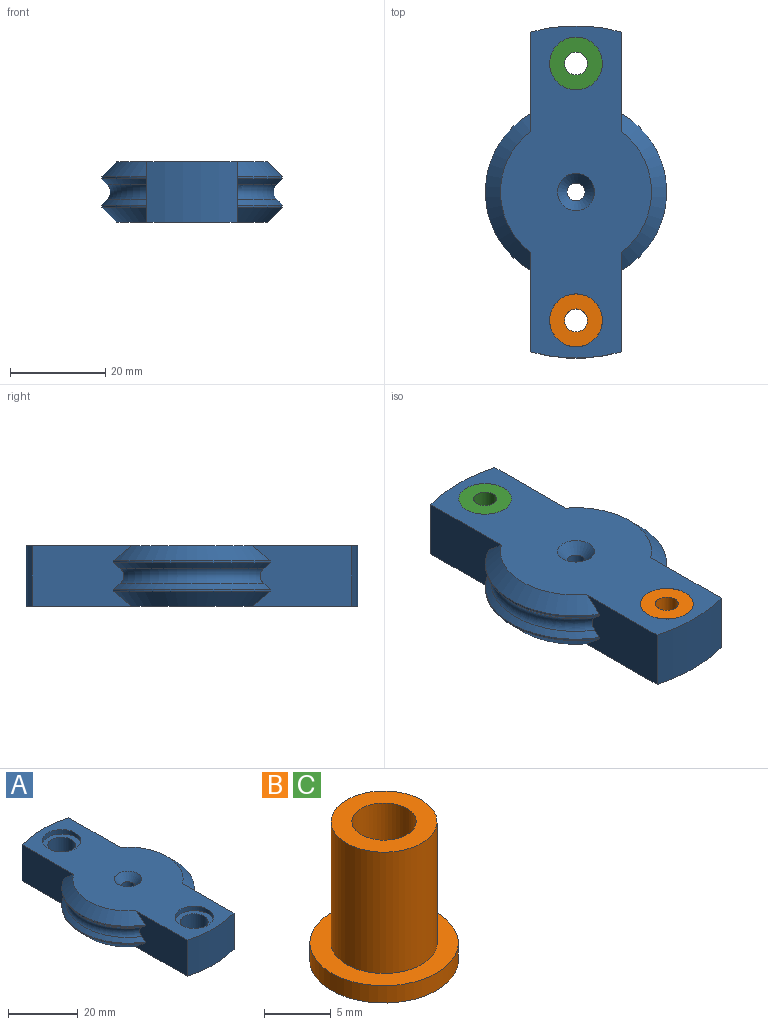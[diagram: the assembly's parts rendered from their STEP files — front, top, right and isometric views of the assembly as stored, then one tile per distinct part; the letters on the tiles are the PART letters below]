
ASSEMBLY  parts=3 mates=2
PART A: 37 faces, bbox 42.2x69.9x12.7 mm
  f0: cylinder r=19.05mm len=33mm, axis (0,0,1), area 14.8mm2, adj f3,f12,f25,f29
  f1: cylinder r=19.05mm len=33mm, axis (0,0,1), area 14.8mm2, adj f8,f14,f23,f26
  f2: plane 69.85x31.75mm, normal (0,0,-1), area 1405.3mm2, adj f3,f6,f8,f9,f12,f13,f14,f15
  f3: plane 20.93x12.73mm, normal (1,0,0), area 237mm2, adj f0,f2,f4,f5,f6,f24,f25,f27
  f4: cylinder r=19.05mm len=33mm, axis (0,0,1), area 14.8mm2, adj f3,f12,f24,f27
  f5: plane 69.85x31.75mm, normal (0,0,1), area 1297.7mm2, adj f3,f6,f8,f11,f12,f13,f14,f17
  f6: cylinder r=34.92mm len=19.05mm, axis (0,0,1), area 245mm2, adj f2,f3,f5,f8
  f7: cylinder r=19.05mm len=33mm, axis (0,0,1), area 14.8mm2, adj f8,f14,f22,f28
  f8: plane 20.93x12.73mm, normal (-1,0,0), area 237mm2, adj f1,f2,f5,f6,f7,f22,f23,f26
  f9: cylinder r=3.99mm len=11.11mm, axis (0,0,1), area 278.4mm2, adj f2,f10
  f10: plane 11.11x11.11mm, normal (0,0,1), area 47mm2, adj f9,f11
  f11: cylinder r=5.56mm len=11.11mm, axis (0,0,1), area 55.4mm2, adj f5,f10
  f12: plane 20.93x12.73mm, normal (1,0,0), area 237mm2, adj f0,f2,f4,f5,f13,f24,f25,f27
  f13: cylinder r=34.92mm len=19.05mm, axis (0,0,1), area 245mm2, adj f2,f5,f12,f14
  f14: plane 20.93x12.73mm, normal (-1,0,0), area 237mm2, adj f1,f2,f5,f7,f13,f22,f23,f26
  f15: cylinder r=3.99mm len=11.11mm, axis (0,0,1), area 278.4mm2, adj f2,f16
  f16: plane 11.11x11.11mm, normal (0,0,1), area 47mm2, adj f15,f17
  f17: cylinder r=5.56mm len=11.11mm, axis (0,0,1), area 55.4mm2, adj f5,f16
  f18: cylinder r=1.1mm len=9.5mm, axis (0,0,-1), area 65.7mm2, adj f19,f34
  f19: plane 2.2x2.2mm, normal (0,0,-1), area 3.8mm2, adj f18
  f20: cylinder r=1.1mm len=9.5mm, axis (0,0,-1), area 65.7mm2, adj f21,f36
  f21: plane 2.2x2.2mm, normal (0,0,-1), area 3.8mm2, adj f20
  f22: cone r=19.05mm half-angle=45deg, axis (0,0,-1), area 63.7mm2, adj f7,f8,f14,f33
  f23: cone r=19.05mm half-angle=45deg, axis (0,0,1), area 63.7mm2, adj f1,f8,f14,f33
  f24: cone r=19.05mm half-angle=45deg, axis (0,0,1), area 63.7mm2, adj f3,f4,f12,f32
  f25: cone r=19.05mm half-angle=45deg, axis (0,0,-1), area 63.7mm2, adj f0,f3,f12,f32
  f26: cone r=15.88mm half-angle=45deg, axis (0,0,-1), area 155.8mm2, adj f1,f5,f8,f14
  f27: cone r=19.05mm half-angle=45deg, axis (0,0,-1), area 155.8mm2, adj f3,f4,f5,f12
  f28: cone r=15.88mm half-angle=45deg, axis (0,0,1), area 155.8mm2, adj f2,f7,f8,f14
  f29: cone r=19.05mm half-angle=45deg, axis (0,0,1), area 155.8mm2, adj f0,f2,f3,f12
  f30: cylinder r=1.9mm len=9.9mm, axis (0,0,1), area 118.1mm2, adj f31,f35
  f31: cone r=1.9mm half-angle=41deg, axis (0,0,1), area 55.5mm2, adj f5,f30
  f32: torus R=19.48mm, axis (0,0,1), area 124.2mm2, adj f3,f12,f24,f25
  f33: torus R=19.48mm, axis (0,0,1), area 124.2mm2, adj f8,f14,f22,f23
  f34: cone r=1.1mm half-angle=45deg, axis (0,0,-1), area 6mm2, adj f2,f18
  f35: cone r=1.9mm half-angle=45deg, axis (0,0,-1), area 9.5mm2, adj f2,f30
  f36: cone r=1.1mm half-angle=45deg, axis (0,0,-1), area 6mm2, adj f2,f20
PART B: 6 faces, bbox 11.1x11.1x12.7 mm
  f0: cylinder r=5.56mm len=11.11mm, axis (0,0,-1), area 55.4mm2, adj f4,f5
  f1: cylinder r=2.41mm len=12.7mm, axis (0,0,-1), area 192mm2, adj f3,f4
  f2: cylinder r=3.97mm len=11.11mm, axis (0,0,-1), area 277.1mm2, adj f3,f5
  f3: plane 7.94x7.94mm, normal (0,0,1), area 31.3mm2, adj f1,f2
  f4: plane 11.11x11.11mm, normal (0,0,-1), area 78.8mm2, adj f0,f1
  f5: plane 11.11x11.11mm, normal (0,0,1), area 47.5mm2, adj f0,f2
PART C: same geometry as B
PLACE A t=(0,0,-64.9)mm
PLACE B rot(axis=(1,0,0),180deg) t=(0,-26.99,12.7)mm
PLACE C rot(axis=(1,0,0),180deg) t=(0,26.99,12.7)mm
MATE fastened C.f0 <-> A.f15  axis (0,0,1) through (0,26.99,12.7)mm
MATE fastened B.f0 <-> A.f9  axis (0,0,1) through (0,-26.99,12.7)mm
